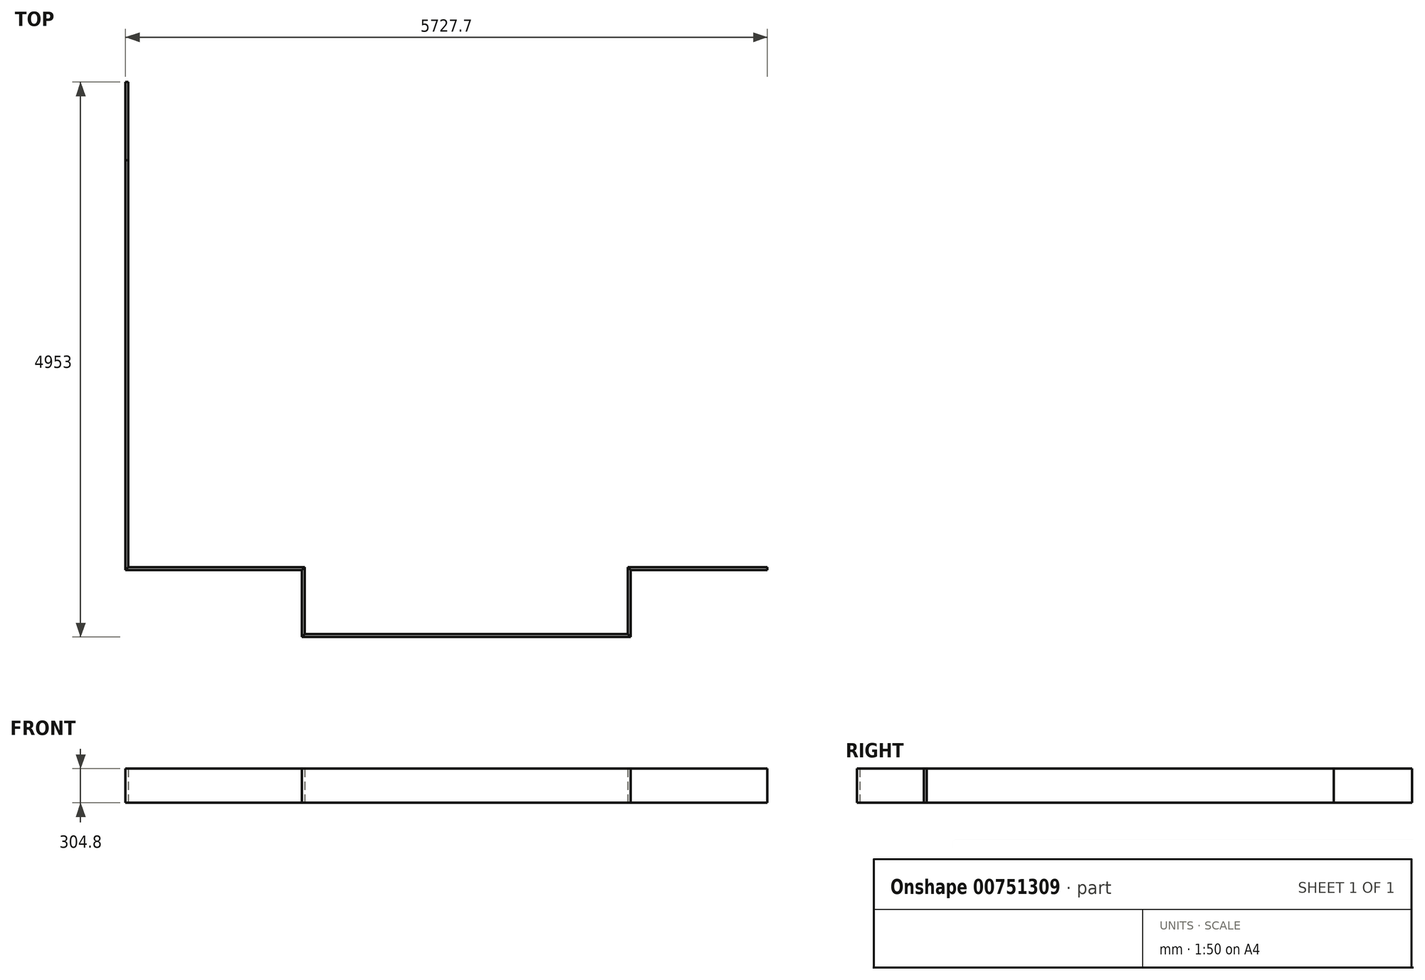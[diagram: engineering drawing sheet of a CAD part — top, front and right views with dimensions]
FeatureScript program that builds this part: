
annotation { "Feature Type Name" : "Feature", "Feature Type Description" : "" }
export const myFeature = defineFeature(function(context is Context, id is Id, definition is map)
    precondition{}
    {
        {
            var Q0;
            Q0=qCreatedBy(makeId("Top.planeOp"),FACE);
            var sketch = newSketch(context, id + "F0", { "sketchPlane" : qUnion([Q0])});
            skLineSegment(sketch, "E0", {"start": v(0, 0) * mm, "end": v(0, 3657.6) * mm});
            skLineSegment(sketch, "E1", {"start": v(0, 3657.6) * mm, "end": v(25.4, 3657.6) * mm});
            skLineSegment(sketch, "E2", {"start": v(25.4, 3657.6) * mm, "end": v(25.4, 25.4) * mm});
            skLineSegment(sketch, "E3", {"start": v(25.4, 25.4) * mm, "end": v(0, 0) * mm});
            skSolve(sketch);
        }
        {
            var Q0;
            Q0 = qSketchRegion(id + "F0", true);
            extrude(context, id + "F1", {"entities" : qUnion([Q0]), "depth" : 304.8 * mm, "offsetDistance" : 25.4 * mm});
        }
        {
            var Q0;
            Q0=qCreatedBy(makeId("Top.planeOp"),FACE);
            var sketch = newSketch(context, id + "F2", { "sketchPlane" : qUnion([Q0])});
            skLineSegment(sketch, "E4", {"start": v(0, 0) * mm, "end": v(1574.8, 0) * mm});
            skLineSegment(sketch, "E5", {"start": v(1574.8, 0) * mm, "end": v(1600.2, 25.4) * mm});
            skLineSegment(sketch, "E6", {"start": v(1600.2, 25.4) * mm, "end": v(25.4, 25.4) * mm});
            skLineSegment(sketch, "E7", {"start": v(25.4, 25.4) * mm, "end": v(0, 0) * mm});
            skSolve(sketch);
        }
        {
            var Q0;
            Q0 = qSketchRegion(id + "F2", true);
            extrude(context, id + "F3", {"entities" : qUnion([Q0]), "depth" : 304.8 * mm, "offsetDistance" : 25.4 * mm});
        }
        {
            var Q0;
            Q0=qCreatedBy(makeId("Top.planeOp"),FACE);
            var sketch = newSketch(context, id + "F4", { "sketchPlane" : qUnion([Q0])});
            skLineSegment(sketch, "E8", {"start": v(1600.2, 25.4) * mm, "end": v(1600.2, -571.5) * mm});
            skLineSegment(sketch, "E9", {"start": v(1600.2, -571.5) * mm, "end": v(1574.8, -596.9) * mm});
            skLineSegment(sketch, "E10", {"start": v(1574.8, -596.9) * mm, "end": v(1574.8, 0) * mm});
            skLineSegment(sketch, "E11", {"start": v(1574.8, 0) * mm, "end": v(1600.2, 25.4) * mm});
            skSolve(sketch);
        }
        {
            var Q0;
            Q0 = qSketchRegion(id + "F4", true);
            extrude(context, id + "F5", {"entities" : qUnion([Q0]), "depth" : 304.8 * mm, "offsetDistance" : 25.4 * mm});
        }
        {
            var Q0;
            Q0=qCreatedBy(makeId("Top.planeOp"),FACE);
            var sketch = newSketch(context, id + "F6", { "sketchPlane" : qUnion([Q0])});
            skLineSegment(sketch, "E12", {"start": v(1574.8, -596.9) * mm, "end": v(4508.5, -596.9) * mm});
            skLineSegment(sketch, "E13", {"start": v(4508.5, -596.9) * mm, "end": v(4483.1, -571.5) * mm});
            skLineSegment(sketch, "E14", {"start": v(4483.1, -571.5) * mm, "end": v(1600.2, -571.5) * mm});
            skLineSegment(sketch, "E15", {"start": v(1600.2, -571.5) * mm, "end": v(1574.8, -596.9) * mm});
            skSolve(sketch);
        }
        {
            var Q0;
            Q0 = qSketchRegion(id + "F6", true);
            extrude(context, id + "F7", {"entities" : qUnion([Q0]), "depth" : 304.8 * mm, "offsetDistance" : 25.4 * mm});
        }
        {
            var Q0;
            Q0=qCreatedBy(makeId("Top.planeOp"),FACE);
            var sketch = newSketch(context, id + "F8", { "sketchPlane" : qUnion([Q0])});
            skLineSegment(sketch, "E16", {"start": v(4508.5, -596.9) * mm, "end": v(4508.5, 0) * mm});
            skLineSegment(sketch, "E17", {"start": v(4483.1, 25.4) * mm, "end": v(4483.1, -571.5) * mm});
            skLineSegment(sketch, "E18", {"start": v(4483.1, -571.5) * mm, "end": v(4508.5, -596.9) * mm});
            skLineSegment(sketch, "E19", {"start": v(4483.1, 25.4) * mm, "end": v(4508.5, 0) * mm});
            skSolve(sketch);
        }
        {
            var Q0;
            Q0 = qSketchRegion(id + "F8", true);
            extrude(context, id + "F9", {"entities" : qUnion([Q0]), "depth" : 304.8 * mm, "offsetDistance" : 25.4 * mm});
        }
        {
            var Q0;
            Q0=qCreatedBy(makeId("Top.planeOp"),FACE);
            var sketch = newSketch(context, id + "F10", { "sketchPlane" : qUnion([Q0])});
            skLineSegment(sketch, "E20", {"start": v(5727.7, 25.4) * mm, "end": v(5727.7, 0) * mm});
            skLineSegment(sketch, "E21", {"start": v(5727.7, 0) * mm, "end": v(4508.5, 0) * mm});
            skLineSegment(sketch, "E22", {"start": v(4508.5, 0) * mm, "end": v(4483.1, 25.4) * mm});
            skLineSegment(sketch, "E23", {"start": v(4483.1, 25.4) * mm, "end": v(5727.7, 25.4) * mm});
            skSolve(sketch);
        }
        {
            var Q0;
            Q0 = qSketchRegion(id + "F10", true);
            extrude(context, id + "F11", {"entities" : qUnion([Q0]), "depth" : 304.8 * mm, "offsetDistance" : 25.4 * mm});
        }
        {
            var Q0;
            Q0=qCreatedBy(makeId("Top.planeOp"),FACE);
            var sketch = newSketch(context, id + "F12", { "sketchPlane" : qUnion([Q0])});
            skLineSegment(sketch, "E24.bottom", {"start": v(0, 3657.6) * mm, "end": v(25.4, 3657.6) * mm});
            skLineSegment(sketch, "E24.top", {"start": v(0, 4356.1) * mm, "end": v(25.4, 4356.1) * mm});
            skLineSegment(sketch, "E24.left", {"start": v(0, 3657.6) * mm, "end": v(0, 4356.1) * mm});
            skLineSegment(sketch, "E24.right", {"start": v(25.4, 3657.6) * mm, "end": v(25.4, 4356.1) * mm});
            skSolve(sketch);
        }
        {
            var Q0;
            Q0 = qSketchRegion(id + "F12", true);
            extrude(context, id + "F13", {"entities" : qUnion([Q0]), "depth" : 304.8 * mm, "offsetDistance" : 25.4 * mm});
        }
    });
